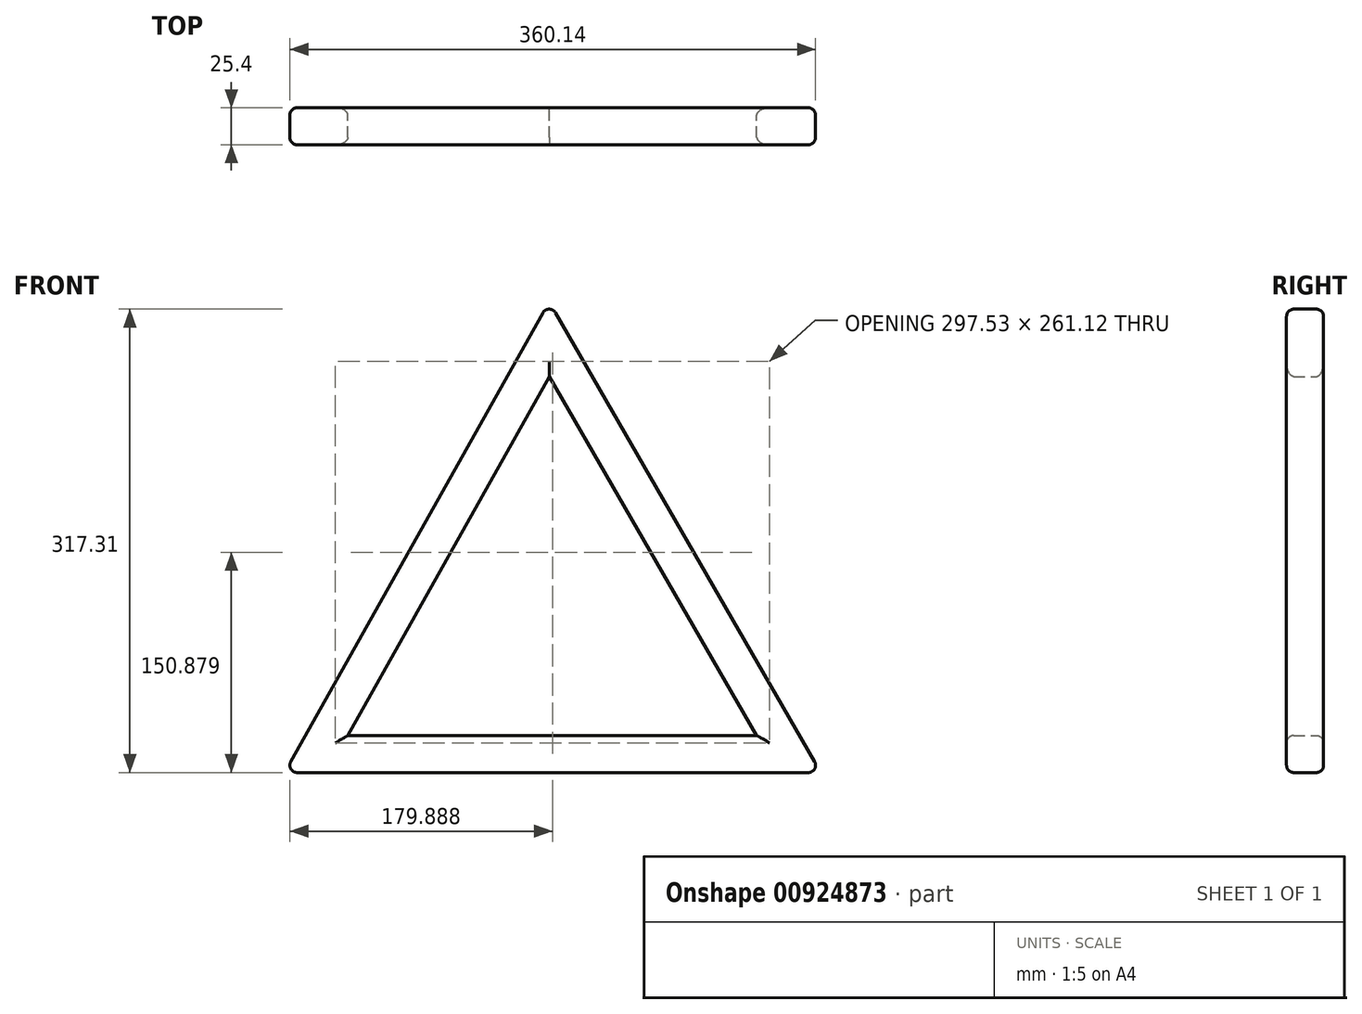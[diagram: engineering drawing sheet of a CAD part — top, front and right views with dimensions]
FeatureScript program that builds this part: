
annotation { "Feature Type Name" : "Feature", "Feature Type Description" : "" }
export const myFeature = defineFeature(function(context is Context, id is Id, definition is map)
    precondition{}
    {
        {
            var Q0;
            Q0=qCreatedBy(makeId("Front.planeOp"),FACE);
            var sketch = newSketch(context, id + "F0", { "sketchPlane" : qUnion([Q0])});
            skLineSegment(sketch, "E0", {"start": v(-181.15, -106.94) * mm, "end": v(0, 215.55) * mm});
            skLineSegment(sketch, "E1", {"start": v(-181.15, -106.94) * mm, "end": v(186.31, -106.94) * mm});
            skLineSegment(sketch, "E2", {"start": v(0, 215.55) * mm, "end": v(186.31, -106.94) * mm});
            skLineSegment(sketch, "E3.0", {"start": v(0.31, 164.24) * mm, "end": v(142.3, -81.54) * mm});
            skLineSegment(sketch, "E4.trimOffspring", {"start": v(-137.75, -81.54) * mm, "end": v(142.3, -81.54) * mm});
            skLineSegment(sketch, "E5.trimOffspring", {"start": v(-137.75, -81.54) * mm, "end": v(0.31, 164.24) * mm});
            skSolve(sketch);
        }
        {
            var Q0;
            Q0=makeQuery(id+"F0.imprint","IMPRINT",FACE,{"disambiguationData":[TD([[makeQuery(id+"F0.imprint","IMPRINT",EDGE,{"derivedFrom":sQuery(id+"F0.wireOp",EDGE,"E0")}),-1.0]])]});
            extrude(context, id + "F1", {"entities" : qUnion([Q0]), "depth" : 25.4 * mm, "offsetDistance" : 25.4 * mm});
        }
        {
            var Q0;
            Q0=makeQuery(id+"F1.opExtrude","CAP_EDGE",EDGE,{"disambiguationData":[OSD([sQuery(id+"F0.wireOp",EDGE,"E2")])],"isStart":true});
            var Q1;
            Q1=makeQuery(id+"F1.opExtrude","CAP_EDGE",EDGE,{"disambiguationData":[OSD([sQuery(id+"F0.wireOp",EDGE,"E0")])],"isStart":true});
            var Q2;
            Q2=makeQuery(id+"F1.opExtrude","CAP_EDGE",EDGE,{"disambiguationData":[OSD([sQuery(id+"F0.wireOp",EDGE,"E1")])],"isStart":true});
            var Q3;
            Q3=makeQuery(id+"F1.opExtrude","CAP_EDGE",EDGE,{"disambiguationData":[OSD([sQuery(id+"F0.wireOp",EDGE,"E4.trimOffspring")])],"isStart":true});
            var Q4;
            Q4=makeQuery(id+"F1.opExtrude","CAP_EDGE",EDGE,{"disambiguationData":[OSD([sQuery(id+"F0.wireOp",EDGE,"E3.0")])],"isStart":true});
            var Q5;
            Q5=makeQuery(id+"F1.opExtrude","CAP_EDGE",EDGE,{"disambiguationData":[OSD([sQuery(id+"F0.wireOp",EDGE,"E5.trimOffspring")])],"isStart":true});
            var Q6;
            Q6=makeQuery(id+"F1.opExtrude","CAP_EDGE",EDGE,{"disambiguationData":[OSD([sQuery(id+"F0.wireOp",EDGE,"E2")])],"isStart":false});
            var Q7;
            Q7=makeQuery(id+"F1.opExtrude","CAP_EDGE",EDGE,{"disambiguationData":[OSD([sQuery(id+"F0.wireOp",EDGE,"E1")])],"isStart":false});
            var Q8;
            Q8=makeQuery(id+"F1.opExtrude","CAP_EDGE",EDGE,{"disambiguationData":[OSD([sQuery(id+"F0.wireOp",EDGE,"E0")])],"isStart":false});
            var Q9;
            Q9=makeQuery(id+"F1.opExtrude","CAP_EDGE",EDGE,{"disambiguationData":[OSD([sQuery(id+"F0.wireOp",EDGE,"E4.trimOffspring")])],"isStart":false});
            var Q10;
            Q10=makeQuery(id+"F1.opExtrude","CAP_EDGE",EDGE,{"disambiguationData":[OSD([sQuery(id+"F0.wireOp",EDGE,"E3.0")])],"isStart":false});
            var Q11;
            Q11=makeQuery(id+"F1.opExtrude","CAP_EDGE",EDGE,{"disambiguationData":[OSD([sQuery(id+"F0.wireOp",EDGE,"E5.trimOffspring")])],"isStart":false});
            var Q12;
            Q12=makeQuery(id+"F1.opExtrude","SWEPT_EDGE",EDGE,{"disambiguationData":[OSD([sQuery(id+"F0.wireOp",EDGE,"E0"),sQuery(id+"F0.wireOp",EDGE,"E2")])]});
            var Q13;
            Q13=makeQuery(id+"F1.opExtrude","SWEPT_EDGE",EDGE,{"disambiguationData":[OSD([sQuery(id+"F0.wireOp",EDGE,"E1"),sQuery(id+"F0.wireOp",EDGE,"E2")])]});
            var Q14;
            Q14=makeQuery(id+"F1.opExtrude","SWEPT_EDGE",EDGE,{"disambiguationData":[OSD([sQuery(id+"F0.wireOp",EDGE,"E0"),sQuery(id+"F0.wireOp",EDGE,"E1")])]});
            fillet(context, id + "F2", {"entities" : qUnion([Q0, Q1, Q2, Q3, Q4, Q5, Q6, Q7, Q8, Q9, Q10, Q11, Q12, Q13, Q14]), "radius" : 5.08 * mm, "tangentPropagation" : true, "allowEdgeOverflow" : false});
        }
    });
